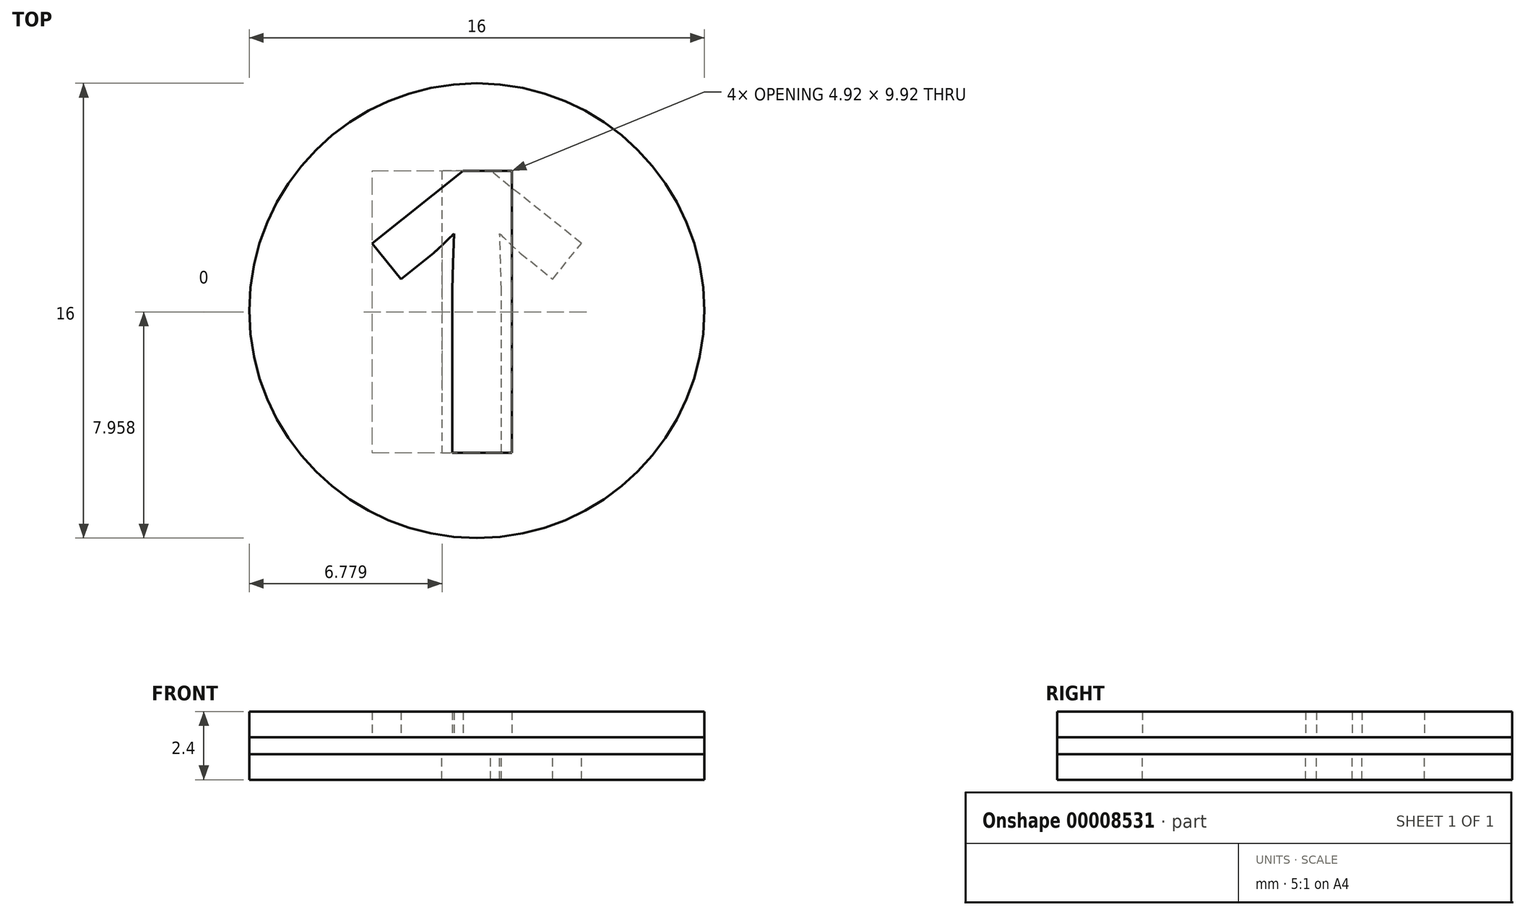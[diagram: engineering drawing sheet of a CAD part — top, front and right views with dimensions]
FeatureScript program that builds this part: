
annotation { "Feature Type Name" : "Feature", "Feature Type Description" : "" }
export const myFeature = defineFeature(function(context is Context, id is Id, definition is map)
    precondition{}
    {
        {
            var Q0;
            Q0=qCreatedBy(makeId("Top.planeOp"),FACE);
            var sketch = newSketch(context, id + "F0", { "sketchPlane" : qUnion([Q0])});
            skCircle(sketch, "E0", {"center": v(0, 0) * mm, "radius": 8 * mm});
            skText(sketch, "E1", { "text": "1", "fontName": "OpenSans-Bold.ttf"});
            skLineSegment(sketch, "E2", {"start": v(-45.5, -5) * mm, "end": v(9.11, -5) * mm, "construction": true});
            skLineSegment(sketch, "E3", {"start": v(0, 0) * mm, "end": v(0, 15.36) * mm, "construction": true});
            const initialGuessF0  = {"E1": [-0.0045, -0.005, 1, 0, 0.01]};
            skSetInitialGuess(sketch, initialGuessF0);
            skSolve(sketch);
        }
        {
            var Q0;
            Q0=makeQuery(id+"F0.imprint","IMPRINT",FACE,{"disambiguationData":[TD([[makeQuery(id+"F0.imprint","IMPRINT",EDGE,{"derivedFrom":sQuery(id+"F0.wireOp",EDGE,"E0")}),1.0]])]});
            extrude(context, id + "F1", {"entities" : qUnion([Q0]), "depth" : 0.9 * mm, "offsetDistance" : 25 * mm});
        }
        {
            var Q0;
            Q0=makeQuery(id+"F0.imprint","IMPRINT",FACE,{"disambiguationData":[TD([[makeQuery(id+"F0.imprint","IMPRINT",EDGE,{"derivedFrom":sQuery(id+"F0.wireOp",EDGE,"E0")}),1.0]])]});
            var Q1;
            Q1=makeQuery(id+"F0.imprint","IMPRINT",FACE,{"disambiguationData":[TD([[makeQuery(id+"F0.imprint","IMPRINT",EDGE,{"derivedFrom":sQuery(id+"F0.wireOp",EDGE,"E1.sketch_text.stroke-0")}),-1.0]])]});
            extrude(context, id + "F2", {"entities" : qUnion([Q0, Q1]), "oppositeDirection" : true, "depth" : 0.6 * mm, "offsetDistance" : 25 * mm});
        }
        {
            var Q0;
            Q0=makeQuery(id+"F1.opExtrude","SWEPT_BODY",BODY,{"disambiguationData":[OSD([sQuery(id+"F0.wireOp",EDGE,"E0"),sQuery(id+"F0.wireOp",EDGE,"E1.sketch_text.stroke-0"),sQuery(id+"F0.wireOp",EDGE,"E1.sketch_text.stroke-1"),sQuery(id+"F0.wireOp",EDGE,"E1.sketch_text.stroke-2"),sQuery(id+"F0.wireOp",EDGE,"E1.sketch_text.stroke-3"),sQuery(id+"F0.wireOp",EDGE,"E1.sketch_text.stroke-4"),sQuery(id+"F0.wireOp",EDGE,"E1.sketch_text.stroke-5"),sQuery(id+"F0.wireOp",EDGE,"E1.sketch_text.stroke-6"),sQuery(id+"F0.wireOp",EDGE,"E1.sketch_text.stroke-7"),sQuery(id+"F0.wireOp",EDGE,"E1.sketch_text.stroke-8"),sQuery(id+"F0.wireOp",EDGE,"E1.sketch_text.stroke-9"),sQuery(id+"F0.wireOp",EDGE,"E1.sketch_text.stroke-10"),sQuery(id+"F0.wireOp",EDGE,"E1.sketch_text.stroke-11"),sQuery(id+"F0.wireOp",EDGE,"E1.sketch_text.stroke-12"),sQuery(id+"F0.wireOp",EDGE,"E1.sketch_text.stroke-13"),sQuery(id+"F0.wireOp",EDGE,"E1.sketch_text.stroke-14"),sQuery(id+"F0.wireOp",EDGE,"E1.sketch_text.stroke-15"),sQuery(id+"F0.wireOp",EDGE,"E1.sketch_text.stroke-16"),sQuery(id+"F0.wireOp",EDGE,"E1.sketch_text.stroke-17"),sQuery(id+"F0.wireOp",EDGE,"E1.sketch_text.stroke-18"),sQuery(id+"F0.wireOp",EDGE,"E1.sketch_text.stroke-19"),sQuery(id+"F0.wireOp",EDGE,"E1.sketch_text.stroke-20"),sQuery(id+"F0.wireOp",EDGE,"E1.sketch_text.stroke-21"),sQuery(id+"F0.wireOp",EDGE,"E1.sketch_text.stroke-22"),sQuery(id+"F0.wireOp",EDGE,"E1.sketch_text.stroke-23")])]});
            transform(context, id + "F3", {"entities" : qUnion([Q0]), "transformType" : TransformType.TRANSLATION_3D, "dx" : 0 * mm, "dy" : 0 * mm, "dz" : 0 * mm, "makeCopy" : true});
        }
        {
            var Q0;
            Q0=makeQuery(id+"F3.opPattern","COPY",BODY,{"derivedFrom":makeQuery(id+"F1.opExtrude","SWEPT_BODY",BODY,{"disambiguationData":[OSD([sQuery(id+"F0.wireOp",EDGE,"E0"),sQuery(id+"F0.wireOp",EDGE,"E1.sketch_text.stroke-0"),sQuery(id+"F0.wireOp",EDGE,"E1.sketch_text.stroke-1"),sQuery(id+"F0.wireOp",EDGE,"E1.sketch_text.stroke-2"),sQuery(id+"F0.wireOp",EDGE,"E1.sketch_text.stroke-3"),sQuery(id+"F0.wireOp",EDGE,"E1.sketch_text.stroke-4"),sQuery(id+"F0.wireOp",EDGE,"E1.sketch_text.stroke-5"),sQuery(id+"F0.wireOp",EDGE,"E1.sketch_text.stroke-6"),sQuery(id+"F0.wireOp",EDGE,"E1.sketch_text.stroke-7"),sQuery(id+"F0.wireOp",EDGE,"E1.sketch_text.stroke-8"),sQuery(id+"F0.wireOp",EDGE,"E1.sketch_text.stroke-9"),sQuery(id+"F0.wireOp",EDGE,"E1.sketch_text.stroke-10"),sQuery(id+"F0.wireOp",EDGE,"E1.sketch_text.stroke-11"),sQuery(id+"F0.wireOp",EDGE,"E1.sketch_text.stroke-12"),sQuery(id+"F0.wireOp",EDGE,"E1.sketch_text.stroke-13"),sQuery(id+"F0.wireOp",EDGE,"E1.sketch_text.stroke-14"),sQuery(id+"F0.wireOp",EDGE,"E1.sketch_text.stroke-15"),sQuery(id+"F0.wireOp",EDGE,"E1.sketch_text.stroke-16"),sQuery(id+"F0.wireOp",EDGE,"E1.sketch_text.stroke-17"),sQuery(id+"F0.wireOp",EDGE,"E1.sketch_text.stroke-18"),sQuery(id+"F0.wireOp",EDGE,"E1.sketch_text.stroke-19"),sQuery(id+"F0.wireOp",EDGE,"E1.sketch_text.stroke-20"),sQuery(id+"F0.wireOp",EDGE,"E1.sketch_text.stroke-21"),sQuery(id+"F0.wireOp",EDGE,"E1.sketch_text.stroke-22"),sQuery(id+"F0.wireOp",EDGE,"E1.sketch_text.stroke-23")])]}),"instanceName":"1"});
            var Q1;
            Q1=sQuery(id+"F0.wireOp",EDGE,"E3");
            transform(context, id + "F4", {"entities" : qUnion([Q0]), "transformType" : TransformType.ROTATION, "transformAxis" : qUnion([Q1]), "angle" : 180 * degree, "makeCopy" : false});
        }
        {
            var Q0;
            Q0=makeQuery(id+"F3.opPattern","COPY",BODY,{"derivedFrom":makeQuery(id+"F1.opExtrude","SWEPT_BODY",BODY,{"disambiguationData":[OSD([sQuery(id+"F0.wireOp",EDGE,"E0"),sQuery(id+"F0.wireOp",EDGE,"E1.sketch_text.stroke-0"),sQuery(id+"F0.wireOp",EDGE,"E1.sketch_text.stroke-1"),sQuery(id+"F0.wireOp",EDGE,"E1.sketch_text.stroke-2"),sQuery(id+"F0.wireOp",EDGE,"E1.sketch_text.stroke-3"),sQuery(id+"F0.wireOp",EDGE,"E1.sketch_text.stroke-4"),sQuery(id+"F0.wireOp",EDGE,"E1.sketch_text.stroke-5"),sQuery(id+"F0.wireOp",EDGE,"E1.sketch_text.stroke-6"),sQuery(id+"F0.wireOp",EDGE,"E1.sketch_text.stroke-7"),sQuery(id+"F0.wireOp",EDGE,"E1.sketch_text.stroke-8"),sQuery(id+"F0.wireOp",EDGE,"E1.sketch_text.stroke-9"),sQuery(id+"F0.wireOp",EDGE,"E1.sketch_text.stroke-10"),sQuery(id+"F0.wireOp",EDGE,"E1.sketch_text.stroke-11"),sQuery(id+"F0.wireOp",EDGE,"E1.sketch_text.stroke-12"),sQuery(id+"F0.wireOp",EDGE,"E1.sketch_text.stroke-13"),sQuery(id+"F0.wireOp",EDGE,"E1.sketch_text.stroke-14"),sQuery(id+"F0.wireOp",EDGE,"E1.sketch_text.stroke-15"),sQuery(id+"F0.wireOp",EDGE,"E1.sketch_text.stroke-16"),sQuery(id+"F0.wireOp",EDGE,"E1.sketch_text.stroke-17"),sQuery(id+"F0.wireOp",EDGE,"E1.sketch_text.stroke-18"),sQuery(id+"F0.wireOp",EDGE,"E1.sketch_text.stroke-19"),sQuery(id+"F0.wireOp",EDGE,"E1.sketch_text.stroke-20"),sQuery(id+"F0.wireOp",EDGE,"E1.sketch_text.stroke-21"),sQuery(id+"F0.wireOp",EDGE,"E1.sketch_text.stroke-22"),sQuery(id+"F0.wireOp",EDGE,"E1.sketch_text.stroke-23")])]}),"instanceName":"1"});
            transform(context, id + "F5", {"entities" : qUnion([Q0]), "transformType" : TransformType.TRANSLATION_3D, "dx" : 0 * mm, "dy" : 0 * mm, "dz" : -0.6 * mm, "makeCopy" : false});
        }
    });
